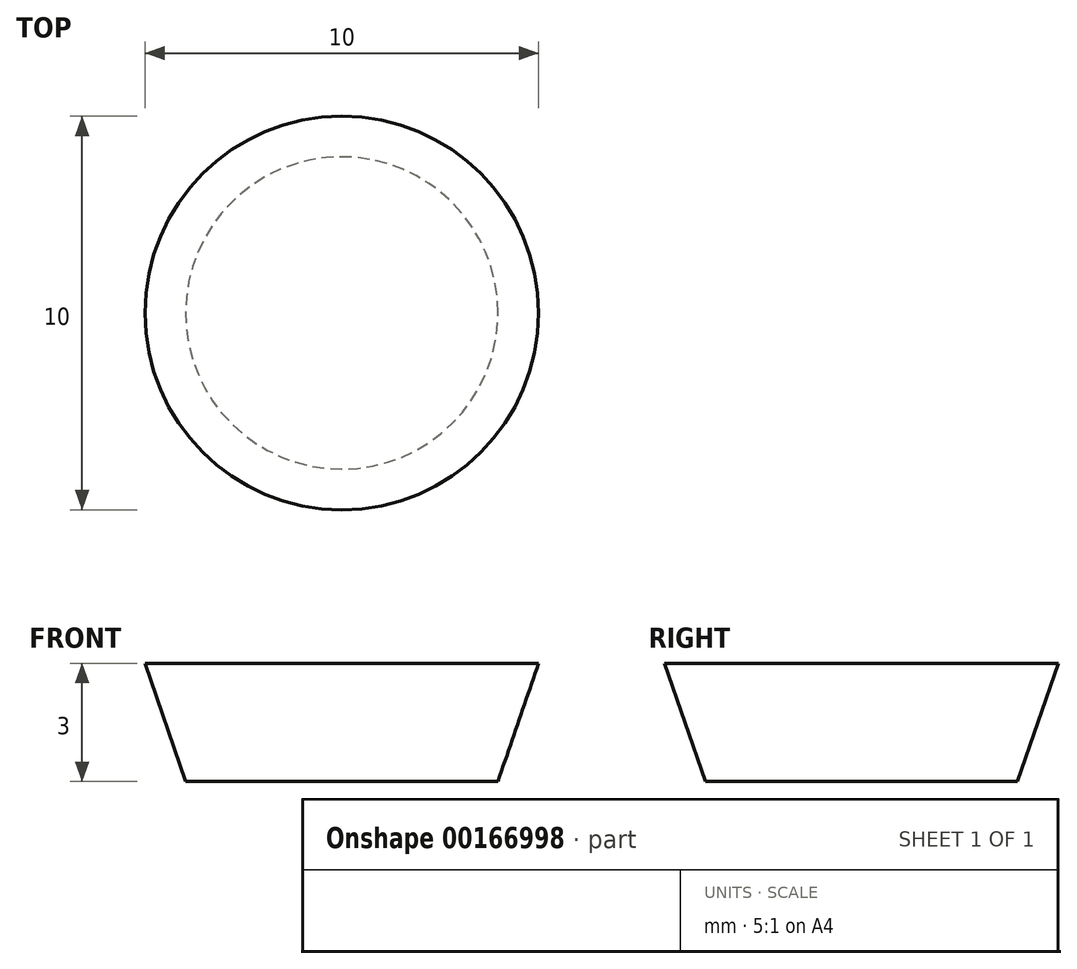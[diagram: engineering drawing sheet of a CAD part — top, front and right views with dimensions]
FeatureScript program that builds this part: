
annotation { "Feature Type Name" : "Feature", "Feature Type Description" : "" }
export const myFeature = defineFeature(function(context is Context, id is Id, definition is map)
    precondition{}
    {
        {
            var Q0;
            Q0=qCreatedBy(makeId("Top.planeOp"),FACE);
            var sketch = newSketch(context, id + "F0", { "sketchPlane" : qUnion([Q0])});
            skCircle(sketch, "E0", {"center": v(0, 0) * mm, "radius": 5 * mm});
            skSolve(sketch);
        }
        {
            var Q0;
            Q0=makeQuery(id+"F0.imprint","IMPRINT",FACE,{"disambiguationData":[TD([[makeQuery(id+"F0.imprint","IMPRINT",EDGE,{"derivedFrom":sQuery(id+"F0.wireOp",EDGE,"E0")}),1.0]])]});
            extrude(context, id + "F1", {"entities" : qUnion([Q0]), "depth" : 3 * mm});
        }
        {
            var Q0;
            Q0=makeQuery(id+"F1.opExtrude","CAP_EDGE",EDGE,{"disambiguationData":[OSD([sQuery(id+"F0.wireOp",EDGE,"E0")])],"isStart":true});
            chamfer(context, id + "F2", {"entities" : qUnion([Q0]), "chamferType" : ChamferType.OFFSET_ANGLE, "width" : 3 * mm, "oppositeDirection" : false, "angle" : 19 * degree, "tangentPropagation" : true});
        }
    });
